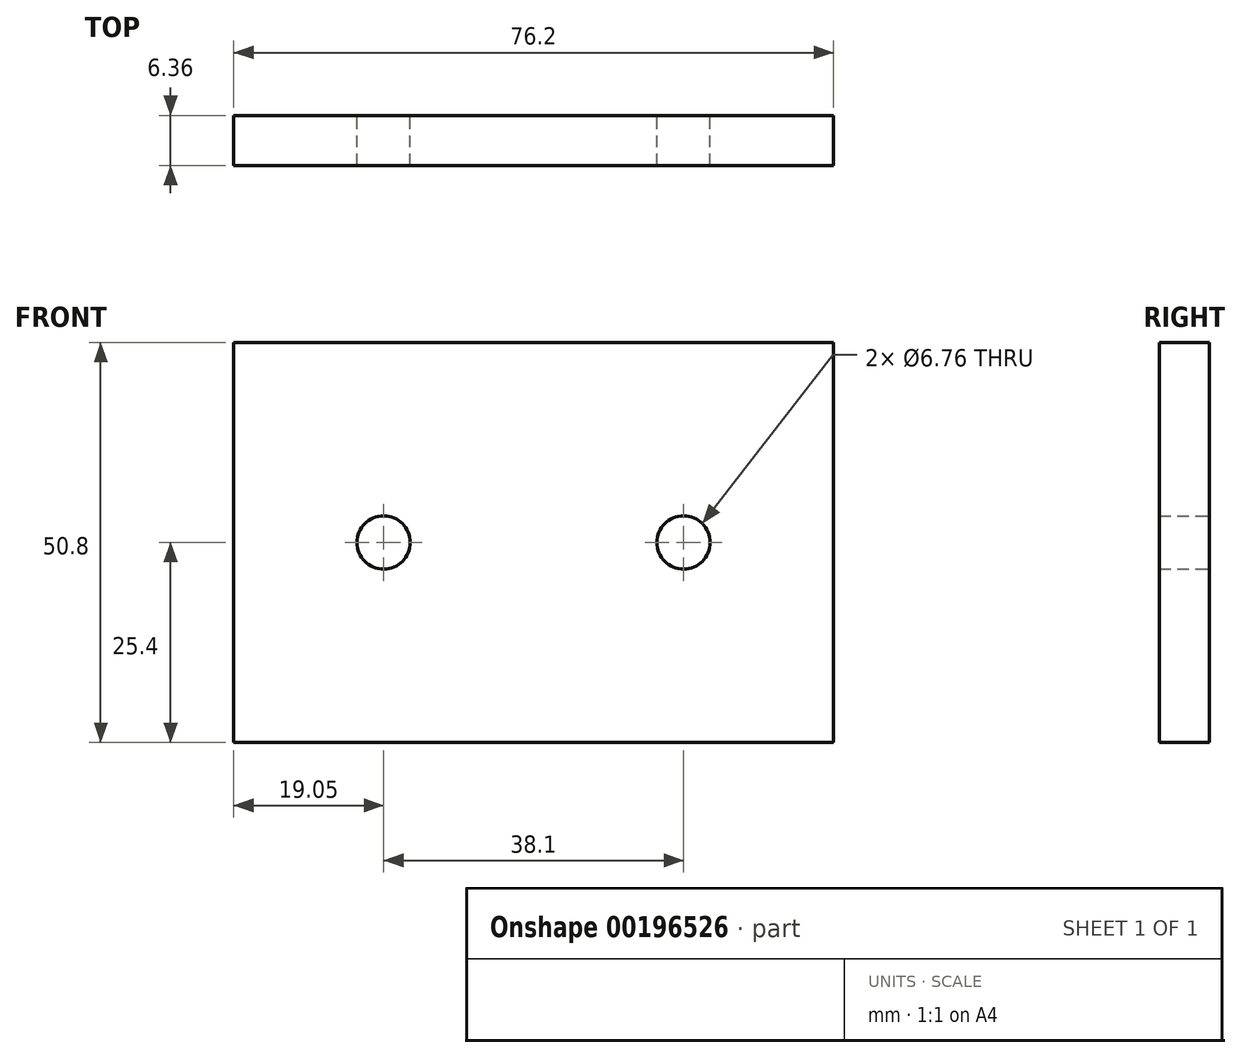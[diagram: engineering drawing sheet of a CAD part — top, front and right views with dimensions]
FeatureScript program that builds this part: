
annotation { "Feature Type Name" : "Feature", "Feature Type Description" : "" }
export const myFeature = defineFeature(function(context is Context, id is Id, definition is map)
    precondition{}
    {
        {
            var Q0;
            Q0=qCreatedBy(makeId("Front.planeOp"),FACE);
            var sketch = newSketch(context, id + "F0", { "sketchPlane" : qUnion([Q0])});
            skLineSegment(sketch, "E0.bottom", {"start": v(38.1, 25.4) * mm, "end": v(-38.1, 25.4) * mm});
            skLineSegment(sketch, "E0.top", {"start": v(38.1, -25.4) * mm, "end": v(-38.1, -25.4) * mm});
            skLineSegment(sketch, "E0.left", {"start": v(38.1, 25.4) * mm, "end": v(38.1, -25.4) * mm});
            skLineSegment(sketch, "E0.right", {"start": v(-38.1, 25.4) * mm, "end": v(-38.1, -25.4) * mm});
            skPoint(sketch, "E0.middle", {"position": v(0, 0) * mm});
            skCircle(sketch, "E1", {"center": v(-19.05, 0) * mm, "radius": 3.38 * mm});
            skCircle(sketch, "E2.MirrorC", {"center": v(19.05, 0) * mm, "radius": 3.38 * mm});
            skSolve(sketch);
        }
        {
            var Q0;
            Q0=makeQuery(id+"F0.imprint","IMPRINT",FACE,{"disambiguationData":[TD([[makeQuery(id+"F0.imprint","IMPRINT",EDGE,{"derivedFrom":sQuery(id+"F0.wireOp",EDGE,"E0.bottom")}),1.0]])]});
            extrude(context, id + "F1", {"entities" : qUnion([Q0]), "endBound" : BoundingType.SYMMETRIC, "depth" : 6.35 * mm});
        }
    });
